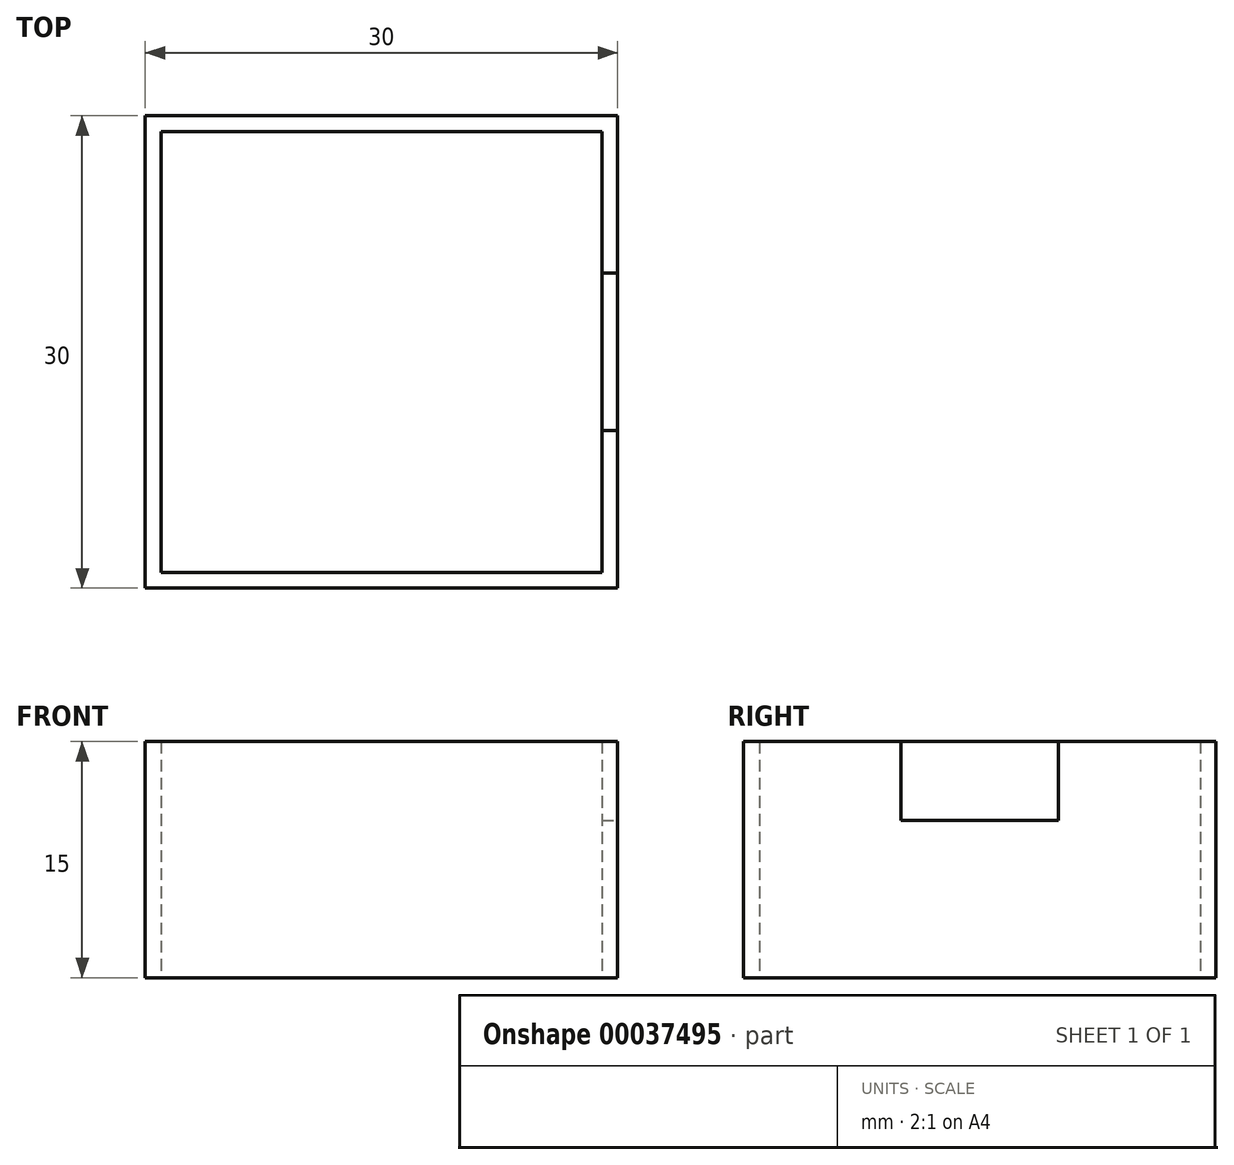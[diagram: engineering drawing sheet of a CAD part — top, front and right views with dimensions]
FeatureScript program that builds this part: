
annotation { "Feature Type Name" : "Feature", "Feature Type Description" : "" }
export const myFeature = defineFeature(function(context is Context, id is Id, definition is map)
    precondition{}
    {
        {
            var Q0;
            Q0=qCreatedBy(makeId("Top.planeOp"),FACE);
            var sketch = newSketch(context, id + "F0", { "sketchPlane" : qUnion([Q0])});
            skLineSegment(sketch, "E0.rect.bottom", {"start": v(15, -15) * mm, "end": v(-15, -15) * mm});
            skLineSegment(sketch, "E0.rect.top", {"start": v(15, 15) * mm, "end": v(-15, 15) * mm});
            skLineSegment(sketch, "E0.rect.left", {"start": v(15, -15) * mm, "end": v(15, 15) * mm});
            skLineSegment(sketch, "E0.rect.right", {"start": v(-15, -15) * mm, "end": v(-15, 15) * mm});
            skPoint(sketch, "E0.rect.middle", {"position": v(0, 0) * mm});
            skLineSegment(sketch, "E1.rect.bottom", {"start": v(14, -14) * mm, "end": v(-14, -14) * mm});
            skLineSegment(sketch, "E1.rect.top", {"start": v(14, 14) * mm, "end": v(-14, 14) * mm});
            skLineSegment(sketch, "E1.rect.left", {"start": v(14, -14) * mm, "end": v(14, 14) * mm});
            skLineSegment(sketch, "E1.rect.right", {"start": v(-14, -14) * mm, "end": v(-14, 14) * mm});
            skSolve(sketch);
        }
        {
            var Q0;
            Q0 = qSketchRegion(id + "F0", true);
            extrude(context, id + "F1", {"entities" : qUnion([Q0]), "depth" : 15 * mm});
        }
        {
            var Q0;
            Q0=makeQuery(id+"F1.opExtrude","SWEPT_FACE",FACE,{"disambiguationData":[OSD([sQuery(id+"F0.wireOp",EDGE,"E0.rect.left")])]});
            var sketch = newSketch(context, id + "F2", { "sketchPlane" : qUnion([Q0])});
            skLineSegment(sketch, "E2.rect.bottom", {"start": v(5, 10) * mm, "end": v(-5, 10) * mm});
            skLineSegment(sketch, "E2.rect.top", {"start": v(5, 20) * mm, "end": v(-5, 20) * mm});
            skLineSegment(sketch, "E2.rect.left", {"start": v(5, 10) * mm, "end": v(5, 20) * mm});
            skLineSegment(sketch, "E2.rect.right", {"start": v(-5, 10) * mm, "end": v(-5, 20) * mm});
            skPoint(sketch, "E2.rect.middle", {"position": v(0, 15) * mm});
            skSolve(sketch);
        }
        {
            var Q0;
            {var subQ5=sQuery(id+"F2.wireOp",EDGE,"E2.rect.top");Q0=makeQuery(id+"F2.imprint","IMPRINT",FACE,{"disambiguationData":[TD([[makeQuery(id+"F2.imprint","IMPRINT",EDGE,{"derivedFrom":subQ5}),1.0]])]});}
            var Q1;
            {var subQ5=sQuery(id+"F2.wireOp",EDGE,"E2.rect.bottom");Q1=makeQuery(id+"F2.imprint","IMPRINT",FACE,{"disambiguationData":[TD([[makeQuery(id+"F2.imprint","IMPRINT",EDGE,{"derivedFrom":subQ5}),-1.0]])]});}
            extrude(context, id + "F3", {"entities" : qUnion([Q0, Q1]), "operationType" : NewBodyOperationType.REMOVE, "oppositeDirection" : true, "depth" : 25 * mm});
        }
    });
